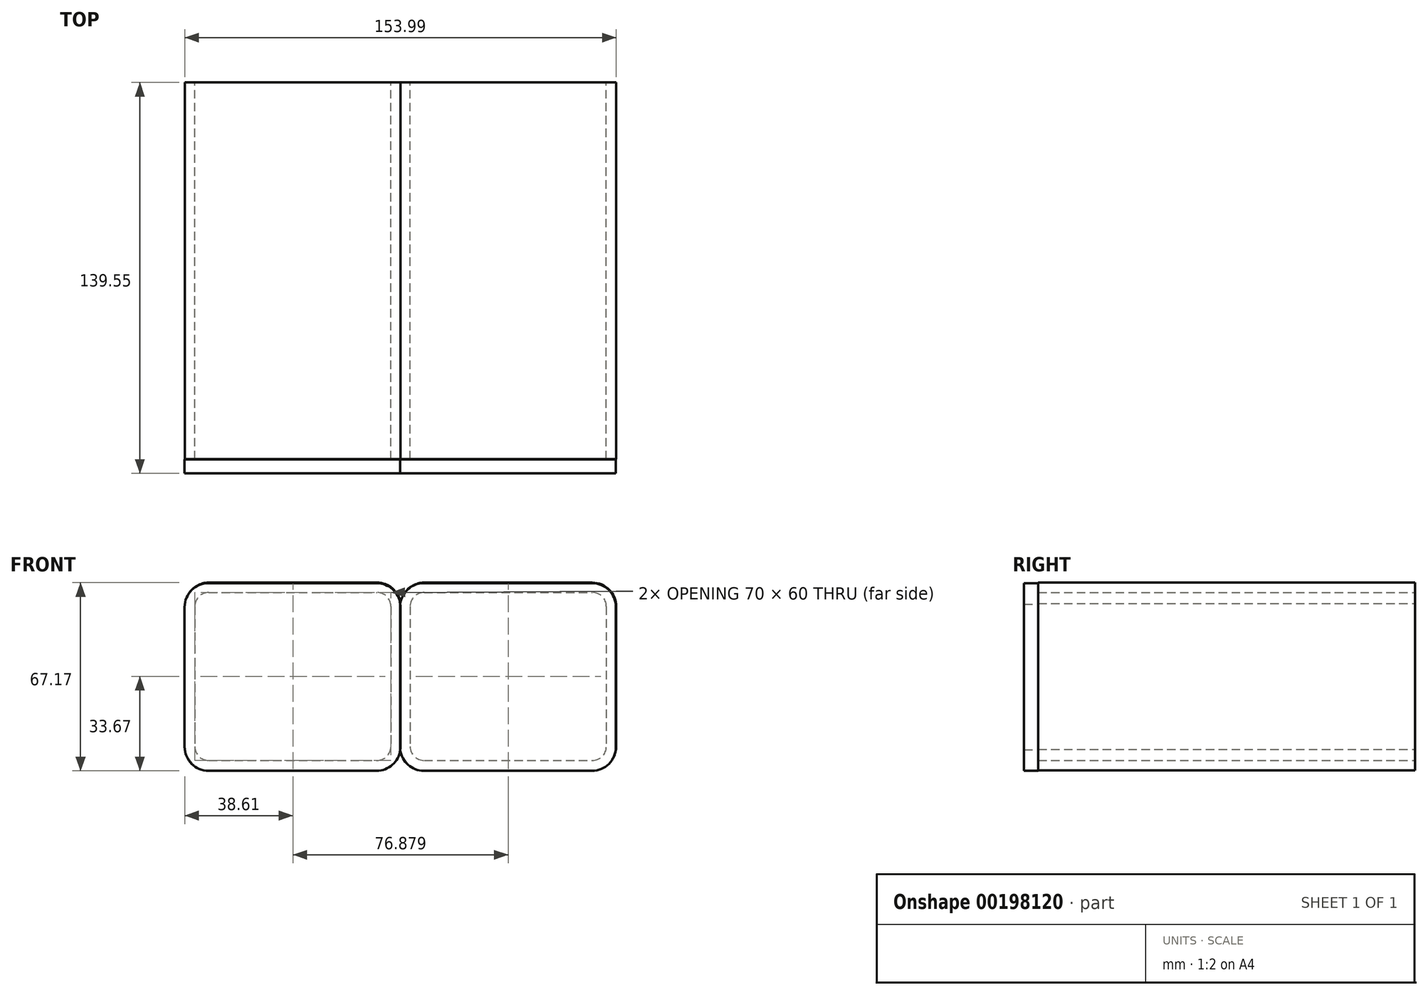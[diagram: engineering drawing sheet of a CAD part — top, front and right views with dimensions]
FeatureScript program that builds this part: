
annotation { "Feature Type Name" : "Feature", "Feature Type Description" : "" }
export const myFeature = defineFeature(function(context is Context, id is Id, definition is map)
    precondition{}
    {
        {
            var Q0;
            Q0=qCreatedBy(makeId("Front.planeOp"),FACE);
            var sketch = newSketch(context, id + "F0", { "sketchPlane" : qUnion([Q0])});
            skLineSegment(sketch, "E0.bottom", {"start": v(-30, 30) * mm, "end": v(30, 30) * mm});
            skLineSegment(sketch, "E0.top", {"start": v(-30, -30) * mm, "end": v(30, -30) * mm});
            skLineSegment(sketch, "E0.left", {"start": v(-35, 25) * mm, "end": v(-35, -25) * mm});
            skLineSegment(sketch, "E0.right", {"start": v(35, 25) * mm, "end": v(35, -25) * mm});
            skPoint(sketch, "E0.middle", {"position": v(0, 0) * mm});
            skPoint(sketch, "E1.visualSharp", {"position": v(-35, -30) * mm});
            skArc(sketch, "E1.filletArc", {"start": v(-35, -25) * mm, "mid": v(-33.54, -28.54) * mm, "end": v(-30, -30) * mm});
            skPoint(sketch, "E2.visualSharp", {"position": v(35, -30) * mm});
            skArc(sketch, "E2.filletArc", {"start": v(30, -30) * mm, "mid": v(33.54, -28.54) * mm, "end": v(35, -25) * mm});
            skPoint(sketch, "E3.visualSharp", {"position": v(35, 30) * mm});
            skArc(sketch, "E3.filletArc", {"start": v(35, 25) * mm, "mid": v(33.54, 28.54) * mm, "end": v(30, 30) * mm});
            skPoint(sketch, "E4.visualSharp", {"position": v(-35, 30) * mm});
            skArc(sketch, "E4.filletArc", {"start": v(-30, 30) * mm, "mid": v(-33.54, 28.54) * mm, "end": v(-35, 25) * mm});
            skArc(sketch, "E5.0", {"start": v(-30, 33.5) * mm, "mid": v(-36.01, 31.01) * mm, "end": v(-38.5, 25) * mm});
            skLineSegment(sketch, "E5.1", {"start": v(-38.5, 25) * mm, "end": v(-38.5, -25) * mm});
            skLineSegment(sketch, "E5.2", {"start": v(-30, 33.5) * mm, "end": v(30, 33.5) * mm});
            skArc(sketch, "E5.3", {"start": v(-38.5, -25) * mm, "mid": v(-36.01, -31.01) * mm, "end": v(-30, -33.5) * mm});
            skArc(sketch, "E5.4", {"start": v(38.5, 25) * mm, "mid": v(36.01, 31.01) * mm, "end": v(30, 33.5) * mm});
            skLineSegment(sketch, "E5.5", {"start": v(38.5, 25) * mm, "end": v(38.5, -25) * mm});
            skArc(sketch, "E5.6", {"start": v(30, -33.5) * mm, "mid": v(36.01, -31.01) * mm, "end": v(38.5, -25) * mm});
            skLineSegment(sketch, "E5.7", {"start": v(-30, -33.5) * mm, "end": v(30, -33.5) * mm});
            skLineSegment(sketch, "E6.bottom", {"start": v(46.88, 30) * mm, "end": v(106.88, 30) * mm});
            skLineSegment(sketch, "E6.top", {"start": v(46.88, -30) * mm, "end": v(106.88, -30) * mm});
            skLineSegment(sketch, "E6.left", {"start": v(41.88, 25) * mm, "end": v(41.88, -25) * mm});
            skLineSegment(sketch, "E6.right", {"start": v(111.88, 25) * mm, "end": v(111.88, -25) * mm});
            skPoint(sketch, "E6.middle", {"position": v(76.88, 0) * mm});
            skPoint(sketch, "E7.visualSharp", {"position": v(41.88, -30) * mm});
            skArc(sketch, "E7.filletArc", {"start": v(41.88, -25) * mm, "mid": v(43.34, -28.54) * mm, "end": v(46.88, -30) * mm});
            skPoint(sketch, "E8.visualSharp", {"position": v(111.88, -30) * mm});
            skArc(sketch, "E8.filletArc", {"start": v(106.88, -30) * mm, "mid": v(110.41, -28.54) * mm, "end": v(111.88, -25) * mm});
            skPoint(sketch, "E9.visualSharp", {"position": v(111.88, 30) * mm});
            skArc(sketch, "E9.filletArc", {"start": v(111.88, 25) * mm, "mid": v(110.41, 28.54) * mm, "end": v(106.88, 30) * mm});
            skPoint(sketch, "E10.visualSharp", {"position": v(41.88, 30) * mm});
            skArc(sketch, "E10.filletArc", {"start": v(46.88, 30) * mm, "mid": v(43.34, 28.54) * mm, "end": v(41.88, 25) * mm});
            skArc(sketch, "E11.0", {"start": v(46.88, 33.5) * mm, "mid": v(40.87, 31.01) * mm, "end": v(38.38, 25) * mm});
            skLineSegment(sketch, "E11.1", {"start": v(38.38, 25) * mm, "end": v(38.38, -25) * mm});
            skLineSegment(sketch, "E11.2", {"start": v(46.88, 33.5) * mm, "end": v(106.88, 33.5) * mm});
            skArc(sketch, "E11.3", {"start": v(38.38, -25) * mm, "mid": v(40.87, -31.01) * mm, "end": v(46.88, -33.5) * mm});
            skArc(sketch, "E11.4", {"start": v(115.38, 25) * mm, "mid": v(112.89, 31.01) * mm, "end": v(106.88, 33.5) * mm});
            skLineSegment(sketch, "E11.5", {"start": v(115.38, 25) * mm, "end": v(115.38, -25) * mm});
            skArc(sketch, "E11.6", {"start": v(106.88, -33.5) * mm, "mid": v(112.89, -31.01) * mm, "end": v(115.38, -25) * mm});
            skLineSegment(sketch, "E11.7", {"start": v(46.88, -33.5) * mm, "end": v(106.88, -33.5) * mm});
            skSolve(sketch);
        }
        {
            var Q0;
            Q0=makeQuery(id+"F0.imprint","IMPRINT",FACE,{"disambiguationData":[TD([[makeQuery(id+"F0.imprint","IMPRINT",EDGE,{"derivedFrom":sQuery(id+"F0.wireOp",EDGE,"E0.bottom")}),1.0]])]});
            var Q1;
            {var subQ0=sQuery(id+"F0.wireOp",EDGE,"E5.5");Q1=makeQuery(id+"F0.imprint","IMPRINT",FACE,{"disambiguationData":[TD([[makeQuery(id+"F0.imprint","IMPRINT",EDGE,{"derivedFrom":subQ0}),1.0]])]});}
            extrude(context, id + "F1", {"entities" : qUnion([Q0, Q1]), "endBound" : BoundingType.SYMMETRIC, "depth" : 134.5 * mm});
        }
        {
            var Q0;
            Q0=qCreatedBy(makeId("Front.planeOp"),FACE);
            cPlane(context, id + "F2", {"entities" : qUnion([Q0]), "cplaneType" : CPlaneType.OFFSET, "offset" : 67.3 * mm, "width" : 150 * mm, "height" : 150 * mm});
        }
        {
            var Q0;
            Q0=qCreatedBy(id+"F2.planeOp",FACE);
            var sketch = newSketch(context, id + "F3", { "sketchPlane" : qUnion([Q0])});
            skPoint(sketch, "E12.middle", {"position": v(-0.11, -0.17) * mm});
            skPoint(sketch, "E13.visualSharp", {"position": v(-35.11, -30.17) * mm});
            skPoint(sketch, "E14.visualSharp", {"position": v(34.89, -30.17) * mm});
            skPoint(sketch, "E15.visualSharp", {"position": v(34.89, 29.83) * mm});
            skPoint(sketch, "E16.visualSharp", {"position": v(-35.11, 29.83) * mm});
            skArc(sketch, "E17.0", {"start": v(-30.11, 33.33) * mm, "mid": v(-36.12, 30.84) * mm, "end": v(-38.61, 24.83) * mm});
            skLineSegment(sketch, "E17.1", {"start": v(-38.61, 24.83) * mm, "end": v(-38.61, -25.17) * mm});
            skLineSegment(sketch, "E17.2", {"start": v(-30.11, 33.33) * mm, "end": v(29.89, 33.33) * mm});
            skArc(sketch, "E17.3", {"start": v(-38.61, -25.17) * mm, "mid": v(-36.12, -31.19) * mm, "end": v(-30.11, -33.67) * mm});
            skArc(sketch, "E17.4", {"start": v(38.39, 24.83) * mm, "mid": v(35.9, 30.84) * mm, "end": v(29.89, 33.33) * mm});
            skLineSegment(sketch, "E17.5", {"start": v(38.39, 24.83) * mm, "end": v(38.39, -25.17) * mm});
            skArc(sketch, "E17.6", {"start": v(29.89, -33.67) * mm, "mid": v(35.9, -31.19) * mm, "end": v(38.39, -25.17) * mm});
            skLineSegment(sketch, "E17.7", {"start": v(-30.11, -33.67) * mm, "end": v(29.89, -33.67) * mm});
            skPoint(sketch, "E18.middle", {"position": v(76.77, -0.17) * mm});
            skPoint(sketch, "E19.visualSharp", {"position": v(41.77, -30.17) * mm});
            skPoint(sketch, "E20.visualSharp", {"position": v(111.77, -30.17) * mm});
            skPoint(sketch, "E21.visualSharp", {"position": v(111.77, 29.83) * mm});
            skPoint(sketch, "E22.visualSharp", {"position": v(41.77, 29.83) * mm});
            skArc(sketch, "E23.0", {"start": v(46.77, 33.33) * mm, "mid": v(40.76, 30.84) * mm, "end": v(38.27, 24.83) * mm});
            skLineSegment(sketch, "E23.1", {"start": v(38.27, 24.83) * mm, "end": v(38.27, -25.17) * mm});
            skLineSegment(sketch, "E23.2", {"start": v(46.77, 33.33) * mm, "end": v(106.77, 33.33) * mm});
            skArc(sketch, "E23.3", {"start": v(38.27, -25.17) * mm, "mid": v(40.76, -31.19) * mm, "end": v(46.77, -33.67) * mm});
            skArc(sketch, "E23.4", {"start": v(115.27, 24.83) * mm, "mid": v(112.78, 30.84) * mm, "end": v(106.77, 33.33) * mm});
            skLineSegment(sketch, "E23.5", {"start": v(115.27, 24.83) * mm, "end": v(115.27, -25.17) * mm});
            skArc(sketch, "E23.6", {"start": v(106.77, -33.67) * mm, "mid": v(112.78, -31.19) * mm, "end": v(115.27, -25.17) * mm});
            skLineSegment(sketch, "E23.7", {"start": v(46.77, -33.67) * mm, "end": v(106.77, -33.67) * mm});
            skSolve(sketch);
        }
        {
            var Q0;
            Q0=makeQuery(id+"F3.imprint","IMPRINT",FACE,{"disambiguationData":[TD([[makeQuery(id+"F3.imprint","IMPRINT",EDGE,{"derivedFrom":sQuery(id+"F3.wireOp",EDGE,"E17.0")}),1.0]])]});
            var Q1;
            {var subQ5=sQuery(id+"F3.wireOp",EDGE,"E17.5");Q1=makeQuery(id+"F3.imprint","IMPRINT",FACE,{"disambiguationData":[TD([[makeQuery(id+"F3.imprint","IMPRINT",EDGE,{"derivedFrom":subQ5}),1.0]])]});}
            extrude(context, id + "F4", {"entities" : qUnion([Q0, Q1]), "depth" : 5 * mm});
        }
    });
